# Revit family: xxxxBasin-Wall_Hung-DXV-Equility-D2007700X.415_Series
name_source: partatom
category: Plumbing Fixtures
units: mm (PartAtom-declared; Revit-internal decimal feet)

## family parameters
Cut with Voids When Loaded = No
Host = Face
OmniClass Number = 23.45.05.14.14
OmniClass Title = Sinks/Lavatories
Part Type = Normal
Room Calculation Point = No
Round Connector Dimension = Use Radius
Shared = Yes

## types (2) — shared parameters
ADA Compliant = Yes
ASME A112.19.2/CSA B45.1 = Yes
Assembly Code = D2010310
Basin Shape = Rectangular
CW Connection = Yes
CWFU = 1.5
Cold Water Connection Height = 19 3/4"
Cold Water Connection Width = 4"
Cold Water Diameter = 1/2"
Cold Water Radius = 1/4"
Default Elevation = 34"
Distance- 2 Holes = 23 5/8"
Drain = Not Included
Finish = Fine Fire Clay-DXV-415-Canvas White
HW Connection = Yes
HWFU = 1.5
Height = 8 9/16"
Hot Water Connection Height = 19 3/4"
Hot Water Connection Width = 4"
Hot Water Diameter = 1/2"
Hot Water Radius = 1/4"
Installation Instruction Link = https://dxv01.blob.core.windows.net
Installation Type = Wall Hung
Length = 17 7/16"
Manufacturer = DXV
Material = Fine Fire Clay-DXV-415-Canvas White
Product Documentation Link = https://dxv01.blob.core.windows.net
Product Page URL = https://www.dxv.com
Revised Date = 11/28/2021
URL = https://www.dxv.com
Vent Connection = No
WFU = 2
Warranty Documentation Link = https://www.dxv.com
Waste Connection = Yes
Waste Connection Diameter = 1 1/4"
Waste Connection Height = 18 1/8"
Waste Connection Radius = 5/8"
Width = 46 3/4"

## per-type parameters (varying)
| type | Description | Single-Hole | Two-Holes | Void- 2 Hole | Void- Single Hole |
| D20077001.415 | Equility 47" Wall-hung Trough Bathroom Sink- Single Faucet Hole | Yes | No | 1/4" | 9" |
| D20077002.415 | Equility 47" Wall-hung Trough Bathroom Sink- Two Faucet Hole | No | Yes | 9" | 1/4" |

note: column(s) folded — value = type name in every type: Model

## geometry (parser evidence)
native form markers: Sweep x2
no freeform markers — native parametric forms only
